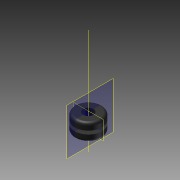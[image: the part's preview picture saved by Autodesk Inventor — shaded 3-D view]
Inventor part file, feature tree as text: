
AUTODESK INVENTOR PART (.ipt)
format: ipt  version: 2016 SP1 (Build 200210100, 210)  size: 134,144 bytes
history: native  units: in
note: dims shown in document units (in); Inventor stores cm internally (conversion verified against a paired STEP export)
features: plane x2, revolve x1, sketch x1, other x1
ambient origin geometry x8: Origin, YZ Plane, XZ Plane, XY Plane, X Axis, Y Axis, Z Axis, Center Point
bodies: Solid1 (feature_tree)
feature tree (5):
  plane  "Work Plane2"
  revolve  "Revolution1"  Angle=90.0deg
  plane  "Work Plane3"
  sketch  "Sketch2"  dims[d0=0.05in d1=90.0deg d2=0.05in d4=0.1562in d5=0.3125in d6=90.0deg]
  other  "Work Axis2"
